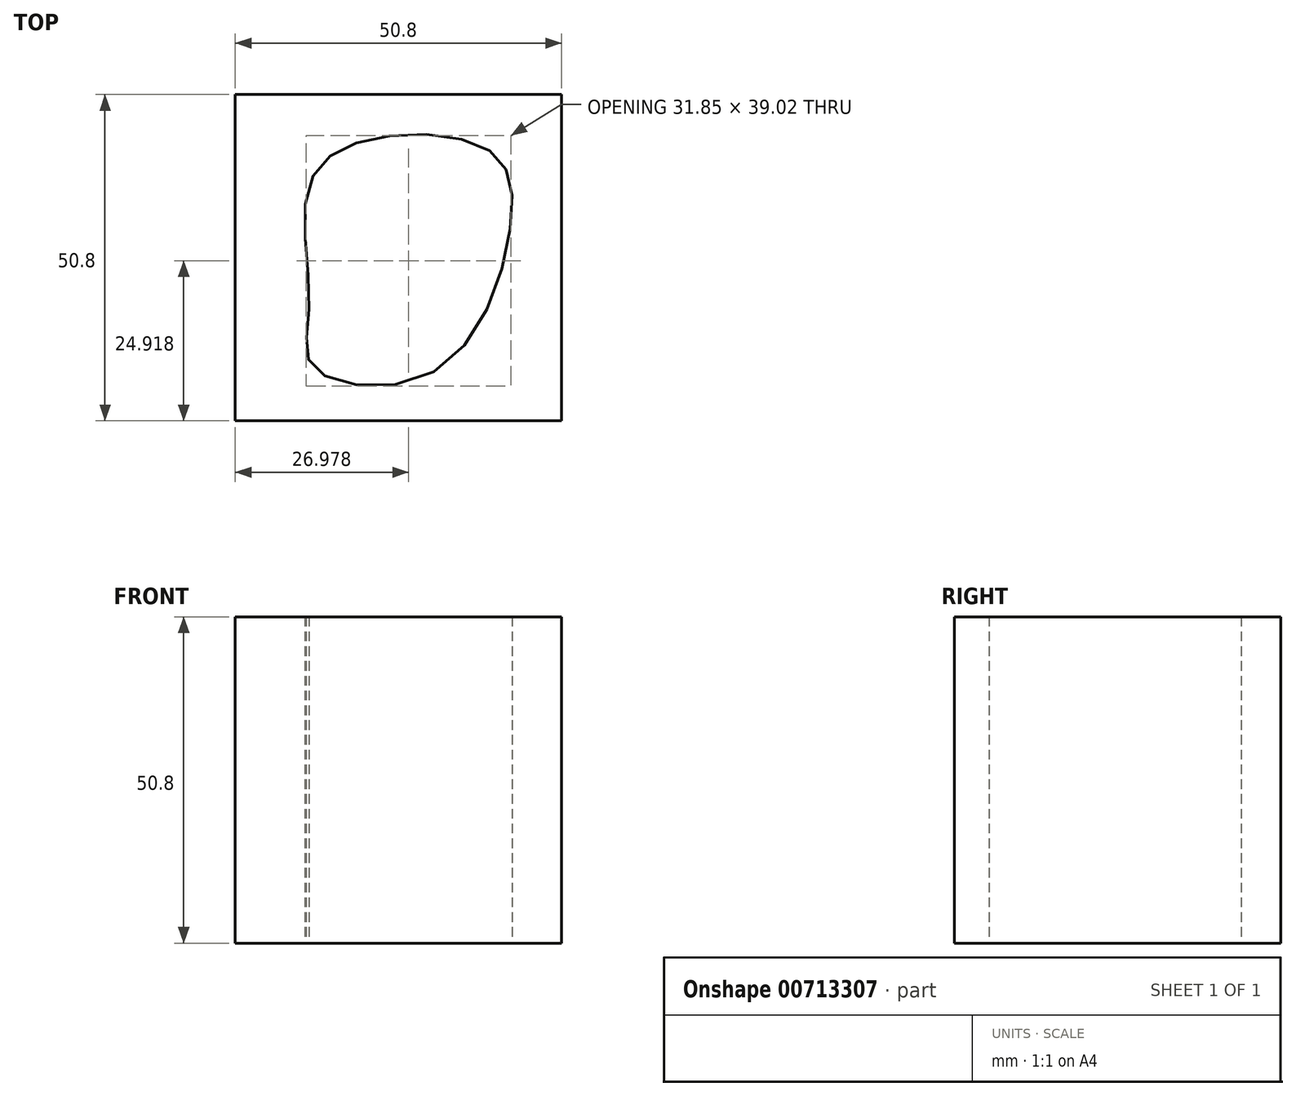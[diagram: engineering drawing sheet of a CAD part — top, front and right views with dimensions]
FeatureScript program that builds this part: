
annotation { "Feature Type Name" : "Feature", "Feature Type Description" : "" }
export const myFeature = defineFeature(function(context is Context, id is Id, definition is map)
    precondition{}
    {
        {
            var Q0;
            Q0=qCreatedBy(makeId("Top.planeOp"),FACE);
            var sketch = newSketch(context, id + "F0", { "sketchPlane" : qUnion([Q0])});
            skLineSegment(sketch, "E0", {"start": v(-25.4, 25.4) * mm, "end": v(-25.4, -25.4) * mm});
            skLineSegment(sketch, "E1", {"start": v(-25.4, -25.4) * mm, "end": v(25.4, -25.4) * mm});
            skLineSegment(sketch, "E2", {"start": v(25.4, -25.4) * mm, "end": v(25.4, 25.4) * mm});
            skLineSegment(sketch, "E3", {"start": v(25.4, 25.4) * mm, "end": v(-25.4, 25.4) * mm});
            skFitSpline(sketch, "E4", {"points": [v(14.18, 16.65) * mm, v(-4.3, 18.47) * mm, v(-13.92, 11.19) * mm, v(-13.92, -7.8) * mm, v(-13.14, -17.17) * mm, v(5.6, -17.7) * mm, v(17.56, 5.72) * mm, v(14.18, 16.65) * mm]});
            skSolve(sketch);
        }
        {
            var Q0;
            Q0=makeQuery(id+"F0.imprint","IMPRINT",FACE,{"disambiguationData":[TD([[makeQuery(id+"F0.imprint","IMPRINT",EDGE,{"derivedFrom":sQuery(id+"F0.wireOp",EDGE,"E0")}),1.0]])]});
            extrude(context, id + "F1", {"entities" : qUnion([Q0]), "depth" : 50.8 * mm, "offsetDistance" : 25.4 * mm});
        }
    });
